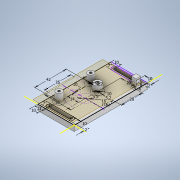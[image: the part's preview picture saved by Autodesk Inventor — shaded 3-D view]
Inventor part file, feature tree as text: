
AUTODESK INVENTOR PART (.ipt)
format: ipt  version: 2022.2 (Build 262287000, 287)  size: 4,137,984 bytes
history: native  units: mm
features: sketch x9, extrude x5, thread x3, revolve x3, helix x3, other x2, hole x1, fillet x1, projected_geometry x1
ambient origin geometry x8: Origin, YZ Plane, XZ Plane, XY Plane, X Axis, Y Axis, Z Axis, Center Point
bodies: Solid2 (feature_tree), Solid3 (feature_tree), Solid4 (feature_tree)
feature tree (28):
  other  "Base Plate"
  sketch  "Sketch1"  dims[d0=10.0mm d1=3.2mm d2=42.0mm d3=8.0mm d4=16.0mm d5=35.0mm d6=35.0mm d7=10.0mm d8=5.2mm d9=7.5mm d10=0.0mm]
  extrude  "Extrusion1"  Depth=10.0mm TaperAngle=0.0deg
  extrude  "Motor Mount"  Depth=3.0mm
  extrude  "Extrusion3"  Depth=11.0mm
  hole  "Hole1"  [1 undecoded]
  extrude  "Extrusion4"  Depth=2.0mm
  extrude  "Extrusion5"  Depth=10.0mm
  thread  "Thread1"  [1 undecoded]
  thread  "Thread2"  [1 undecoded]
  thread  "Thread3"  [1 undecoded]
  other  "Wire Plane"
  fillet  "Fillet1"  Radius=10.0mm
  revolve  "Revolution1"  [1 undecoded]
  helix  "Coil1"  [1 undecoded]
  revolve  "Revolution2"  [1 undecoded]
  helix  "Coil2"  [1 undecoded]
  revolve  "Revolution3"  [1 undecoded]
  helix  "Coil3"  [1 undecoded]
  sketch  "Sketch3"  dims[d11=12.0mm d12=0.0mm d13=3.0mm]
  projected_geometry  "Projected Loop1"
  sketch  "Sketch4"  dims[d14=16.0mm d15=11.0mm]
  sketch  "Sketch5"  dims[d16=14.0mm d17=12.0mm d18=0.0mm]
  sketch  "Sketch6"  dims[d19=3.0mm d20=6.0mm d21=6.0mm d22=2.0mm d23=90.0deg d24=8.0mm d25=0.0mm d26=20.0mm]
  sketch  "Sketch7"  dims[d27=6.0mm d28=6.0mm d29=28.0mm d30=7.0mm d31=2.0mm d32=10.0mm]
  sketch  "Sketch8"  dims[d33=10.0mm d34=1.5mm d35=3.5mm d36=0.0mm]
  sketch  "Sketch9"  dims[d37=10.0mm d38=0.0mm d39=17.5mm d40=0.0mm d41=19.5mm d42=0.0mm]
  sketch  "Sketch10"  dims[d43=19.5mm d44=0.0mm d45=7.0mm d48=2.0mm d49=10.0mm d50=10.0mm d51=1.5mm d52=2.0mm d56=9.599311mm d57=0.128066mm d58=0.128066mm d61=0.8mm d63=9.599311mm d65=0.0mm d66=0.8008mm d67=19.1mm d68=10.0mm d69=0.0mm d70=0.0mm d71=0.0mm d72=0.0mm d73=0.0mm d74=9.599311mm d75=0.080042mm d76=0.080042mm d79=0.5mm d81=9.599311mm d83=0.0mm d84=0.5005mm d85=20.5mm d86=10.0mm d87=0.0mm d88=0.0mm d89=0.0mm d90=0.0mm d91=0.0mm d92=9.599311mm d93=0.080042mm d94=0.080042mm d97=0.5mm d99=9.599311mm d101=0.0mm d102=0.5005mm d103=20.5mm d104=10.0mm d105=0.0mm d106=0.0mm d107=0.0mm d108=0.0mm d109=0.0mm]
note: 10 required parameter values undecoded (feature->parameter linkage not recoverable at this tier; creation-order binding heuristic only, values carry confidence <= 0.55)